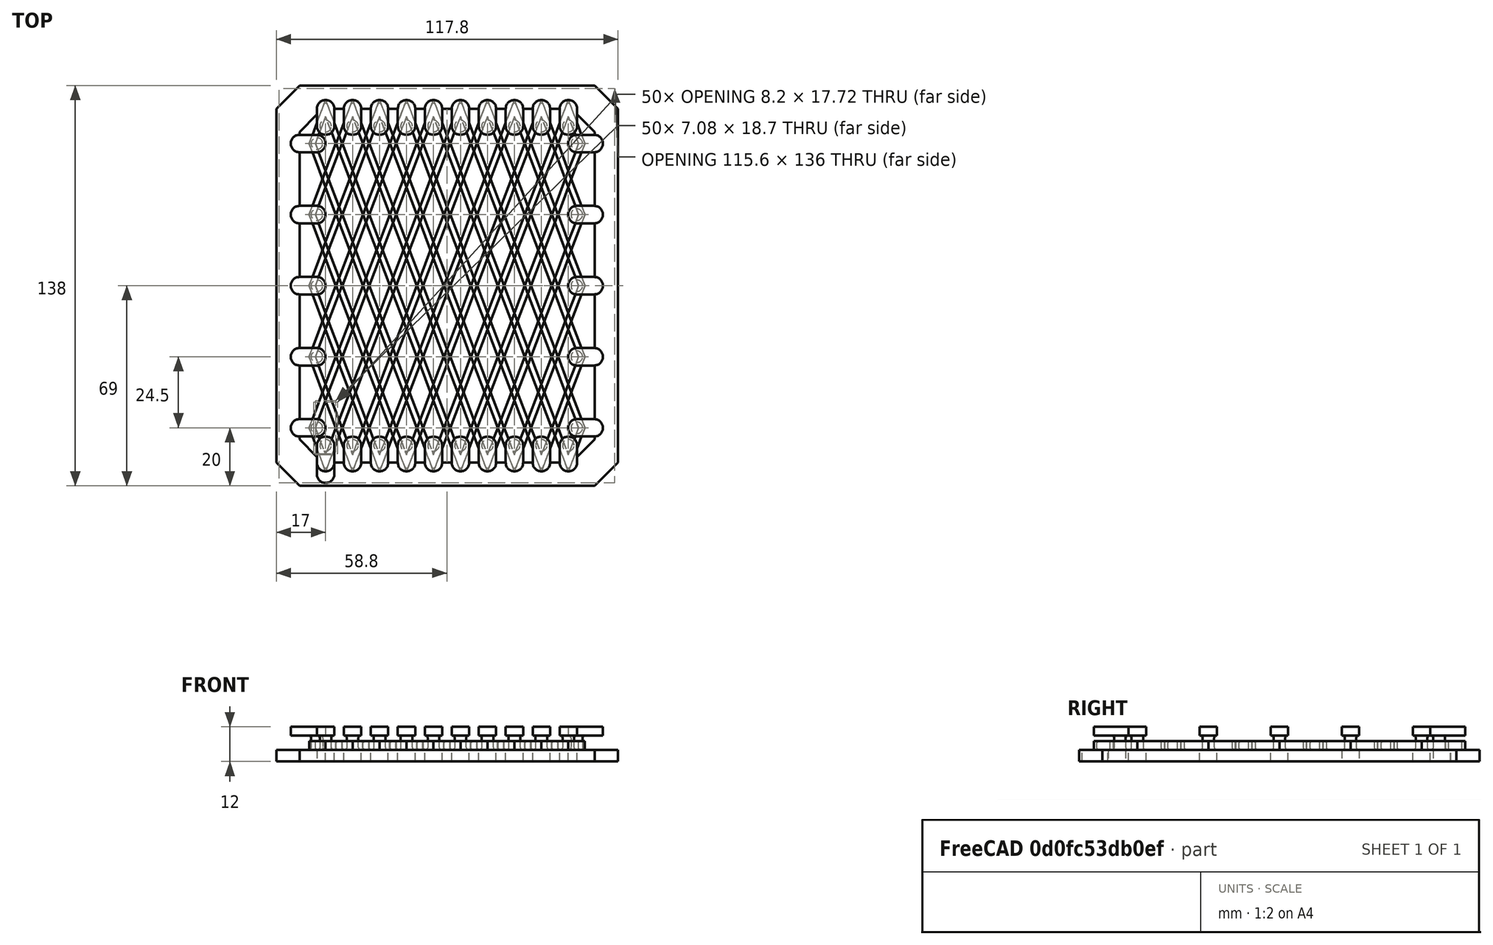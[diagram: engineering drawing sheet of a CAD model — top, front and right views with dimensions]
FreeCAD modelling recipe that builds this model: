
FCSTD DOCUMENT  (FreeCAD 0.16R6348 (Git))
Label: flownet
License: All rights reserved
LicenseURL: http://en.wikipedia.org/wiki/All_rights_reserved
objects: Sketcher::SketchObject×8, PartDesign::Pad×8, PartDesign::Fillet×4, Part::FeaturePython×3, Part::Feature×2, Part::Mirroring×2, Part::Fillet×1, PartDesign::Chamfer×1, Part::MultiFuse×1
note: 38 computed .brp shape members not serialized (recipe doc carries the construction recipe); baked Part::Feature solids carry a one-line shape summary decoded from their .brp

FEATURE [Sketcher::SketchObject] Sketch
  sketch-geometry (8):
    g0: LineSegment StartX=0 StartY=9.35204 StartZ=0 EndX=-3.5411 EndY=0 EndZ=0
    g1: LineSegment StartX=-3.5411 StartY=0 StartZ=0 EndX=0 EndY=-9.35204 EndZ=0
    g2: LineSegment StartX=0 StartY=-9.35204 StartZ=0 EndX=3.5411 EndY=0 EndZ=0
    g3: LineSegment StartX=3.5411 StartY=0 StartZ=0 EndX=0 EndY=9.35204 EndZ=0
    g4: LineSegment StartX=0 StartY=15 StartZ=0 EndX=5.67967 EndY=0 EndZ=0
    g5: LineSegment StartX=5.67967 StartY=0 StartZ=0 EndX=0 EndY=-15 EndZ=0
    g6: LineSegment StartX=0 StartY=-15 StartZ=0 EndX=-5.67967 EndY=0 EndZ=0
    g7: LineSegment StartX=-5.67967 StartY=0 StartZ=0 EndX=0 EndY=15 EndZ=0
  constraints (23):
    c: Coincident(g0,g1)
    c: Coincident(g1,g2)
    c: Coincident(g2,g3)
    c: Coincident(g0,g3)
    c: Equal(g2,g3)
    c: Equal(g3,g0)
    c: Equal(g0,g1)
    c: PointOnObject(g0,g-2)
    c: Symmetric(g1,g0,g-1)
    c: Distance(g3) = 10
    c: Coincident(g4,g5)
    c: Coincident(g5,g6)
    c: Coincident(g6,g7)
    c: Coincident(g4,g7)
    c: PointOnObject(g4,g-2)
    c: Equal(g4,g5)
    c: Equal(g5,g6)
    c: Equal(g6,g7)
    c: PointOnObject(g5,g-2)
    c: Parallel(g4,g3)
    c: Distance(g2,g4) = 2
    c: Symmetric(g5,g4,g-1)
    c: Distance(g-1,g4) = 15
FEATURE [PartDesign::Pad] Pad
  Length = 3
  Length2 = 100
  Sketch = -> Sketch
  Type = 0
FEATURE [Part::FeaturePython] Array  # Draft array (typed FeaturePython)
  Angle = 360
  ArrayType = 0
  Axis = (0,0,1)
  Base = -> Pad
  Center = (0,0,0)
  Fuse = false
  IntervalAxis = (0,0,0)
  IntervalX = (9.3,0,0)
  IntervalY = (0,24.5,0)
  IntervalZ = (0,0,0)
  NumberPolar = 5
  NumberX = 10
  NumberY = 5
  NumberZ = 1
FEATURE [Part::Feature] Array001
  shape: bbox 95.06 x 128 x 3 mm, 500 faces, 50 solids (baked)
FEATURE [Part::Fillet] Fillet
  Base = -> Array001
  Edges = 1200 edges r=0.6: [Edge1,Edge2,Edge3,Edge4,Edge5,Edge6,Edge7,Edge8,Edge9,Edge10,Edge11,Edge12,Edge13,Edge14,Edge15,Edge16,Edge17,Edge18,Edge19,Edge20,Edge21,Edge22,Edge23,Edge24,Edge25,Edge26,Edge27,Edge28,Edge29,Edge30,Edge31,Edge32,Edge33,Edge34,Edge35,Edge36,Edge37,Edge38,Edge39,Edge40,Edge41,Edge42,Edge43,Edge44,+1156 more]
FEATURE [Sketcher::SketchObject] Sketch001
  sketch-geometry (4):
    g0: ArcOfCircle CenterX=0 CenterY=-6 CenterZ=0 NormalX=0 NormalY=0 NormalZ=1 Radius=3 StartAngle=0 EndAngle=3.14159
    g1: ArcOfCircle CenterX=0 CenterY=-16 CenterZ=0 NormalX=0 NormalY=0 NormalZ=1 Radius=3 StartAngle=3.14159 EndAngle=6.28319
    g2: LineSegment StartX=-3 StartY=-6 StartZ=0 EndX=-3 EndY=-16 EndZ=0
    g3: LineSegment StartX=3 StartY=-6 StartZ=0 EndX=3 EndY=-16 EndZ=0
  constraints (10):
    c: Tangent(g0,g3) = 1.5708
    c: Tangent(g0,g2) = -1.5708
    c: Tangent(g2,g1) = -1.5708
    c: Tangent(g3,g1) = 1.5708
    c: Vertical(g2)
    c: Equal(g0,g1)
    c: PointOnObject(g0,g-2)
    c: Radius(g0) = 3
    c: DistanceY(g0) = -6
    c: Distance(g3) = 10
FEATURE [PartDesign::Pad] Pad001
  Length = 4
  Length2 = 100
  Reversed = true
  Sketch = -> Sketch001
  Type = 0
FEATURE [Sketcher::SketchObject] Sketch002
  ExternalGeometry = -> [Pad001]
  Support = -> Pad001 [Face5]
  sketch-geometry (1):
    g0: Circle CenterX=0 CenterY=-6 CenterZ=0 NormalX=0 NormalY=0 NormalZ=1 Radius=2
  constraints (2):
    c: Coincident(g0,g-3)
    c: Radius(g0) = 2
FEATURE [PartDesign::Pad] Pad002
  Length = 5
  Length2 = 100
  Sketch = -> Sketch002
  Type = 0
FEATURE [Sketcher::SketchObject] Sketch003
  ExternalGeometry = -> [Pad002]
  Placement = pos=(0,0,5) rot=(0,0,1;0rad)
  Support = -> Pad002 [Face8]
  sketch-geometry (4):
    g0: ArcOfCircle CenterX=0 CenterY=-6 CenterZ=0 NormalX=0 NormalY=0 NormalZ=1 Radius=3 StartAngle=0 EndAngle=3.14159
    g1: ArcOfCircle CenterX=0 CenterY=-12 CenterZ=0 NormalX=0 NormalY=0 NormalZ=1 Radius=3 StartAngle=3.14159 EndAngle=6.28319
    g2: LineSegment StartX=-3 StartY=-6 StartZ=0 EndX=-3 EndY=-12 EndZ=0
    g3: LineSegment StartX=3 StartY=-6 StartZ=0 EndX=3 EndY=-12 EndZ=0
  constraints (10):
    c: Tangent(g0,g3) = 1.5708
    c: Tangent(g0,g2) = -1.5708
    c: Tangent(g2,g1) = -1.5708
    c: Tangent(g3,g1) = 1.5708
    c: Vertical(g2)
    c: PointOnObject(g0,g-2)
    c: Coincident(g0,g-3)
    c: Distance(g3) = 6
    c: Vertical(g3)
    c: Radius(g0) = 3
FEATURE [PartDesign::Pad] Pad003
  Length = 3
  Length2 = 100
  Sketch = -> Sketch003
  Type = 0
FEATURE [PartDesign::Fillet] Fillet001
  Base = -> Pad003 [Edge15]
  Radius = 0.9
FEATURE [PartDesign::Fillet] Fillet002
  Base = -> Fillet001 [Edge3]
  Radius = 0.9
FEATURE [Part::FeaturePython] Array002  # Draft array (typed FeaturePython)
  Angle = 360
  ArrayType = 0
  Axis = (0,0,1)
  Base = -> Fillet002
  Center = (0,0,0)
  Fuse = false
  IntervalAxis = (0,0,0)
  IntervalX = (9.3,0,0)
  IntervalY = (0,1,0)
  IntervalZ = (0,0,0)
  NumberPolar = 1
  NumberX = 10
  NumberY = 1
  NumberZ = 1
FEATURE [Part::Mirroring] Part__Mirroring  label="Array002 (Mirror #1)"
  Base = (0,49,0)
  Normal = (0,1,0)
  Source = -> Array002
FEATURE [Sketcher::SketchObject] Sketch004
  sketch-geometry (4):
    g0: ArcOfCircle CenterX=0 CenterY=-6 CenterZ=0 NormalX=0 NormalY=0 NormalZ=1 Radius=3 StartAngle=0 EndAngle=3.14159
    g1: ArcOfCircle CenterX=0 CenterY=-16 CenterZ=0 NormalX=0 NormalY=0 NormalZ=1 Radius=3 StartAngle=3.14159 EndAngle=6.28319
    g2: LineSegment StartX=-3 StartY=-6 StartZ=0 EndX=-3 EndY=-16 EndZ=0
    g3: LineSegment StartX=3 StartY=-6 StartZ=0 EndX=3 EndY=-16 EndZ=0
  constraints (10):
    c: Tangent(g0,g3) = 1.5708
    c: Tangent(g0,g2) = -1.5708
    c: Tangent(g2,g1) = -1.5708
    c: Tangent(g3,g1) = 1.5708
    c: Vertical(g2)
    c: Equal(g0,g1)
    c: PointOnObject(g0,g-2)
    c: Radius(g0) = 3
    c: DistanceY(g0) = -6
    c: Distance(g3) = 10
FEATURE [PartDesign::Pad] Pad004
  Length = 4
  Length2 = 100
  Reversed = true
  Sketch = -> Sketch004
  Type = 0
FEATURE [Sketcher::SketchObject] Sketch005
  ExternalGeometry = -> [Pad004]
  Support = -> Pad004 [Face5]
  sketch-geometry (1):
    g0: Circle CenterX=0 CenterY=-6 CenterZ=0 NormalX=0 NormalY=0 NormalZ=1 Radius=2
  constraints (2):
    c: Coincident(g0,g-3)
    c: Radius(g0) = 2
FEATURE [PartDesign::Pad] Pad005
  Length = 5
  Length2 = 100
  Sketch = -> Sketch005
  Type = 0
FEATURE [Sketcher::SketchObject] Sketch006
  ExternalGeometry = -> [Pad005]
  Placement = pos=(0,0,5) rot=(0,0,1;0rad)
  Support = -> Pad005 [Face8]
  sketch-geometry (4):
    g0: ArcOfCircle CenterX=0 CenterY=-6 CenterZ=0 NormalX=0 NormalY=0 NormalZ=1 Radius=3 StartAngle=0 EndAngle=3.14159
    g1: ArcOfCircle CenterX=0 CenterY=-12 CenterZ=0 NormalX=0 NormalY=0 NormalZ=1 Radius=3 StartAngle=3.14159 EndAngle=6.28319
    g2: LineSegment StartX=-3 StartY=-6 StartZ=0 EndX=-3 EndY=-12 EndZ=0
    g3: LineSegment StartX=3 StartY=-6 StartZ=0 EndX=3 EndY=-12 EndZ=0
  constraints (10):
    c: Tangent(g0,g3) = 1.5708
    c: Tangent(g0,g2) = -1.5708
    c: Tangent(g2,g1) = -1.5708
    c: Tangent(g3,g1) = 1.5708
    c: Vertical(g2)
    c: PointOnObject(g0,g-2)
    c: Coincident(g0,g-3)
    c: Distance(g3) = 6
    c: Vertical(g3)
    c: Radius(g0) = 3
FEATURE [PartDesign::Pad] Pad006
  Length = 3
  Length2 = 100
  Sketch = -> Sketch006
  Type = 0
FEATURE [PartDesign::Fillet] Fillet003
  Base = -> Pad006 [Edge15]
  Radius = 0.9
FEATURE [PartDesign::Fillet] Fillet004
  Base = -> Fillet003 [Edge3]
  Radius = 0.9
FEATURE [Part::Feature] Fillet004001  label="Fillet005"
  Placement = pos=(3,0,0) rot=(0,0,-1;1.5708rad)
  shape: bbox 16.83 x 7.661 x 12 mm, 15 faces (baked)
FEATURE [Part::FeaturePython] Array003  # Draft array (typed FeaturePython)
  Angle = 360
  ArrayType = 0
  Axis = (0,0,1)
  Base = -> Fillet004001
  Center = (0,0,0)
  Fuse = false
  IntervalAxis = (0,0,0)
  IntervalX = (1,0,0)
  IntervalY = (0,24.5,0)
  IntervalZ = (0,0,0)
  NumberPolar = 1
  NumberX = 1
  NumberY = 5
  NumberZ = 1
FEATURE [Part::Mirroring] Part__Mirroring001  label="Array003 (Mirror #2)"
  Base = (41.8,0,0)
  Normal = (1,0,0)
  Source = -> Array003
FEATURE [Sketcher::SketchObject] Sketch007
  Placement = pos=(0,0,0) rot=(-1,0,0;3.14159rad)
  sketch-geometry (8):
    g0: LineSegment StartX=-17 StartY=20 StartZ=0 EndX=100.8 EndY=20 EndZ=0
    g1: LineSegment StartX=100.8 StartY=20 StartZ=0 EndX=100.8 EndY=-118 EndZ=0
    g2: LineSegment StartX=100.8 StartY=-118 StartZ=0 EndX=-17 EndY=-118 EndZ=0
    g3: LineSegment StartX=-17 StartY=-118 StartZ=0 EndX=-17 EndY=20 EndZ=0
    g4: LineSegment StartX=-9 StartY=12 StartZ=0 EndX=92.8 EndY=12 EndZ=0
    g5: LineSegment StartX=92.8 StartY=12 StartZ=0 EndX=92.8 EndY=-110 EndZ=0
    g6: LineSegment StartX=92.8 StartY=-110 StartZ=0 EndX=-9 EndY=-110 EndZ=0
    g7: LineSegment StartX=-9 StartY=-110 StartZ=0 EndX=-9 EndY=12 EndZ=0
  constraints (24):
    c: Coincident(g0,g1)
    c: Coincident(g1,g2)
    c: Coincident(g2,g3)
    c: Coincident(g3,g0)
    c: Horizontal(g0)
    c: Horizontal(g2)
    c: Vertical(g1)
    c: Vertical(g3)
    c: Coincident(g4,g5)
    c: Coincident(g5,g6)
    c: Coincident(g6,g7)
    c: Coincident(g7,g4)
    c: Horizontal(g4)
    c: Horizontal(g6)
    c: Vertical(g5)
    c: Vertical(g7)
    c: DistanceX(g0) = -17
    c: DistanceY(g0) = 20
    c: Distance(g0) = 117.8
    c: Distance(g3) = 138
    c: Distance(g6,g2) = 8
    c: Distance(g6,g3) = 8
    c: Distance(g5,g1) = 8
    c: Distance(g4,g0) = 8
FEATURE [PartDesign::Pad] Pad007
  Length = 4
  Length2 = 100
  Placement = pos=(0,0,0) rot=(-1,0,0;3.14159rad)
  Sketch = -> Sketch007
  Type = 0
FEATURE [PartDesign::Chamfer] Chamfer
  Base = -> Pad007 [Edge8,Edge20,Edge13,Edge1,Edge2,Edge14,Edge5,Edge17]
  Placement = pos=(0,0,0) rot=(-1,0,0;3.14159rad)
  Size = 8
FEATURE [Part::MultiFuse] Fusion
  Shapes = -> [Part__Mirroring001,Array002,Part__Mirroring,Array003,Chamfer]
